# Revit family: EKF_EE_ДержательПластроновFORT_PROxima
name_source: partatom
category: Электрооборудование
units: mm (PartAtom-declared; Revit-internal decimal feet)

## family parameters
Всегда вертикально = Нет
На основе рабочей плоскости = Да
Общий = Да
При загрузке вырезать с полостями = Нет
Размер круглого соединителя = Использовать диаметр
Тип детали = Силовой щит
Точка расчета площади = Нет

## types (5) — shared parameters
ADSK_Единица измерения = шт.
ADSK_Завод-изготовитель = EKF
ADSK_Количество = 1
ADSK_Марка = Держатель пластронов FORT
ADSK_Материал = Сталь_Оцинкованная
ADSK_Обозначение = Держатель пластронов FORT
ADSK_Размер_Глубина = 26.7 мм
ADSK_Размер_Ширина = 20 мм
t = 1.2 мм
Изготовитель = EKF
Серия номенклатуры = PROxima
Степень защиты IP = -
ТВ = EKF_2
Тип установки = -
zero-valued in all types: ADSK_Масса, Отметка по умолчанию

## per-type parameters (varying)
| type | ADSK_Код изделия | ADSK_Размер_Высота | Тип |
| Держатель пластронов FORT высотой 2200 (2шт) EKF PROxima | FDP22 | 2189 мм | 322 мм |
| Держатель пластронов FORT высотой 1000 (2шт.) EKF PROxima | FDP10 | 989 мм | 323 мм |
| Держатель пластронов FORT высотой 1800 (2шт) EKF PROxima | FDP18 | 1789 мм | 324 мм |
| Держатель пластронов FORT высотой 2000 (2шт) EKF PROxima | FDP20 | 1989 мм | 325 мм |
| Держатель пластронов FORT высотой 600 (2шт.) EKF PROxima | FDP6 | 589 мм | 326 мм |

note: column(s) folded — value = type name in every type: ADSK_Наименование
